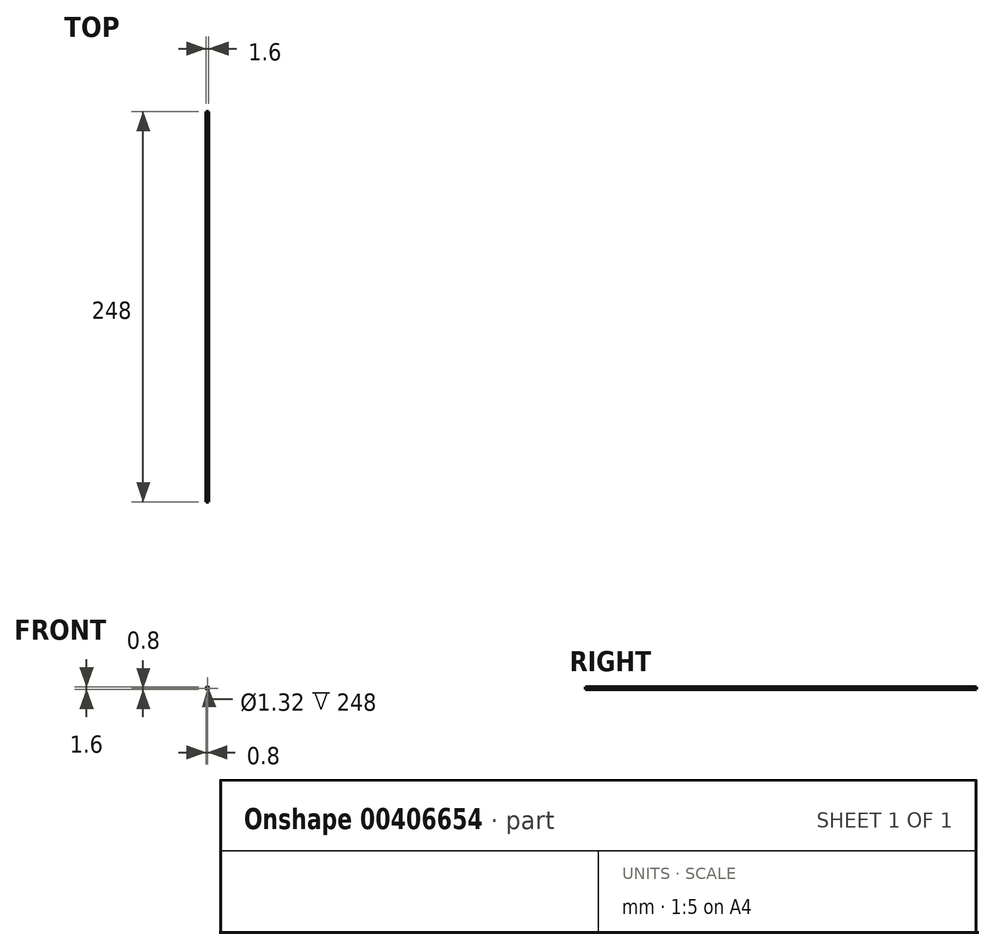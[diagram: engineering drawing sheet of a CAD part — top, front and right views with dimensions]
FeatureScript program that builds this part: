
annotation { "Feature Type Name" : "Feature", "Feature Type Description" : "" }
export const myFeature = defineFeature(function(context is Context, id is Id, definition is map)
    precondition{}
    {
        {
            var Q0;
            Q0=qCreatedBy(makeId("Front.planeOp"),FACE);
            var sketch = newSketch(context, id + "F0", { "sketchPlane" : qUnion([Q0])});
            skCircle(sketch, "E0", {"center": v(0, 0) * mm, "radius": 0.8 * mm});
            skCircle(sketch, "E1.0", {"center": v(0, 0) * mm, "radius": 0.66 * mm});
            skSolve(sketch);
        }
        {
            var Q0;
            Q0=qSketchRegion(id+"F0",true);
            extrude(context, id + "F1", {"entities" : qUnion([Q0]), "oppositeDirection" : true, "depth" : 248 * mm});
        }
    });
